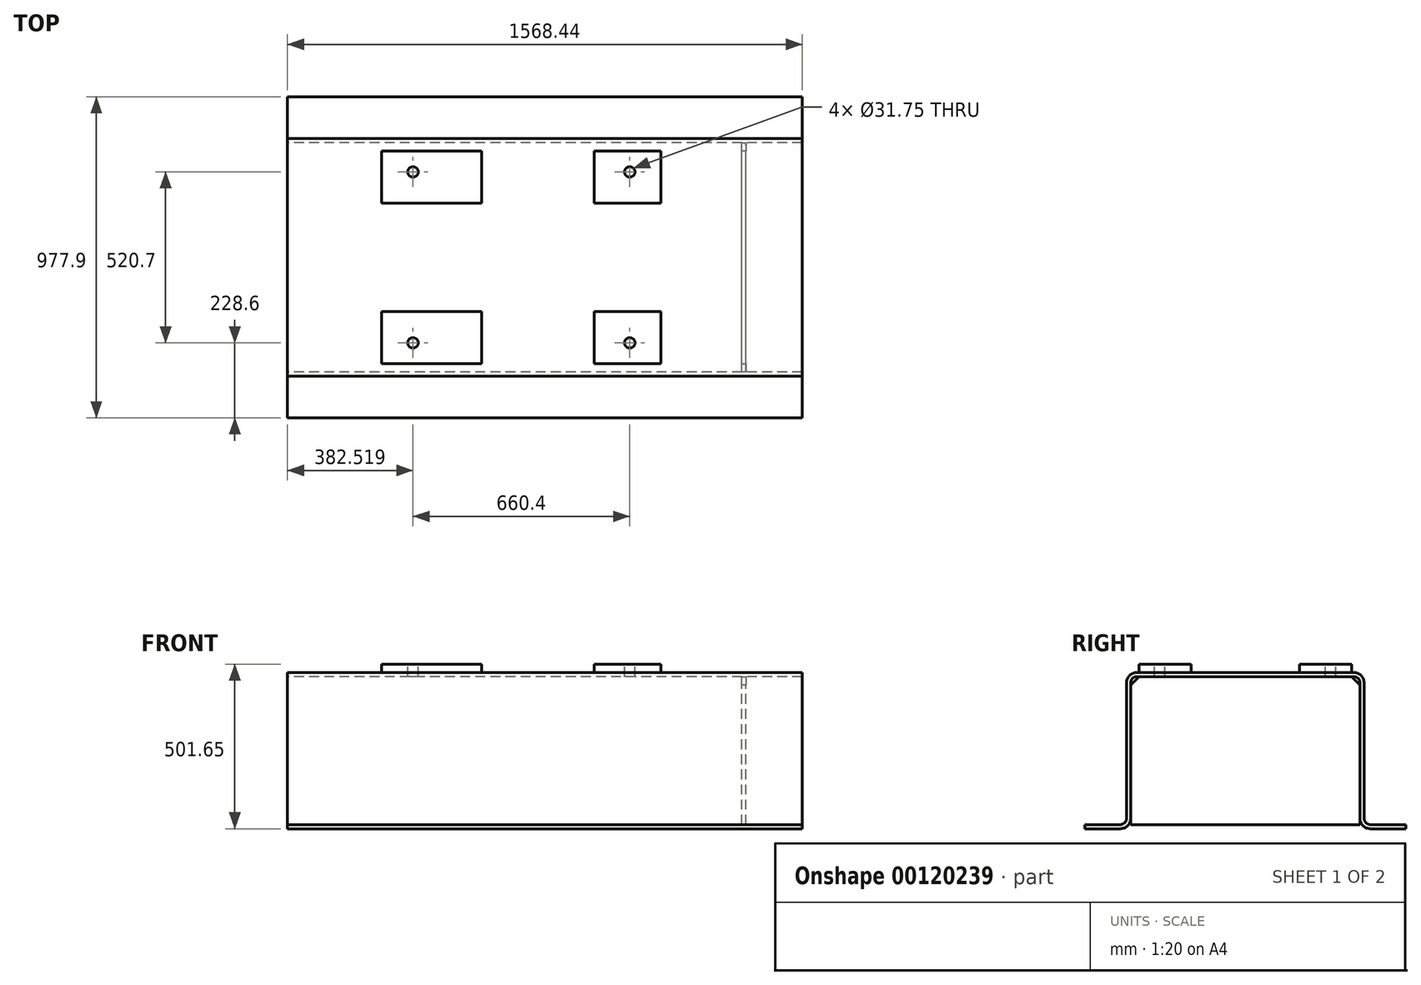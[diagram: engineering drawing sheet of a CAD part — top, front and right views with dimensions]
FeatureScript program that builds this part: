
annotation { "Feature Type Name" : "Feature", "Feature Type Description" : "" }
export const myFeature = defineFeature(function(context is Context, id is Id, definition is map)
    precondition{}
    {
        {
            var Q0;
            Q0=qCreatedBy(makeId("Right.planeOp"),FACE);
            var sketch = newSketch(context, id + "F0", { "sketchPlane" : qUnion([Q0])});
            skLineSegment(sketch, "E0", {"start": v(-488.95, 0) * mm, "end": v(-381, 0) * mm});
            skLineSegment(sketch, "E1", {"start": v(0, -90.03) * mm, "end": v(0, 519.57) * mm, "construction": true});
            skLineSegment(sketch, "E2.0", {"start": v(-361.95, 31.75) * mm, "end": v(-361.95, 444.5) * mm});
            skLineSegment(sketch, "E3.0", {"start": v(-349.25, 31.75) * mm, "end": v(-349.25, 444.5) * mm});
            skPoint(sketch, "E4.orphan", {"position": v(-143.9, 0) * mm});
            skLineSegment(sketch, "E5.0", {"start": v(-488.95, 0) * mm, "end": v(-488.95, 12.7) * mm});
            skLineSegment(sketch, "E6.0", {"start": v(-488.95, 12.7) * mm, "end": v(-381, 12.7) * mm});
            skLineSegment(sketch, "E7.0", {"start": v(-330.2, 476.25) * mm, "end": v(0, 476.25) * mm});
            skLineSegment(sketch, "E8.0", {"start": v(-330.2, 463.55) * mm, "end": v(0, 463.55) * mm});
            skArc(sketch, "E9.filletArc", {"start": v(-381, 12.7) * mm, "mid": v(-367.53, 18.28) * mm, "end": v(-361.95, 31.75) * mm});
            skArc(sketch, "E10.filletArc", {"start": v(-330.2, 463.55) * mm, "mid": v(-343.67, 457.97) * mm, "end": v(-349.25, 444.5) * mm});
            skArc(sketch, "E11.filletArc", {"start": v(-330.2, 476.25) * mm, "mid": v(-352.65, 466.95) * mm, "end": v(-361.95, 444.5) * mm});
            skArc(sketch, "E12.filletArc", {"start": v(-381, 0) * mm, "mid": v(-358.55, 9.3) * mm, "end": v(-349.25, 31.75) * mm});
            skArc(sketch, "E13.MirrorCS", {"start": v(330.2, 463.55) * mm, "mid": v(343.67, 457.97) * mm, "end": v(349.25, 444.5) * mm});
            skLineSegment(sketch, "E14.MirrorCS", {"start": v(361.95, 31.75) * mm, "end": v(361.95, 444.5) * mm});
            skLineSegment(sketch, "E15.MirrorCS", {"start": v(349.25, 31.75) * mm, "end": v(349.25, 444.5) * mm});
            skArc(sketch, "E16.MirrorCS", {"start": v(330.2, 476.25) * mm, "mid": v(352.65, 466.95) * mm, "end": v(361.95, 444.5) * mm});
            skLineSegment(sketch, "E17.MirrorCS", {"start": v(330.2, 463.55) * mm, "end": v(0, 463.55) * mm});
            skLineSegment(sketch, "E18.MirrorCS", {"start": v(330.2, 476.25) * mm, "end": v(0, 476.25) * mm});
            skArc(sketch, "E19.MirrorCS", {"start": v(381, 12.7) * mm, "mid": v(367.53, 18.28) * mm, "end": v(361.95, 31.75) * mm});
            skLineSegment(sketch, "E20.MirrorCS", {"start": v(488.95, 0) * mm, "end": v(488.95, 12.7) * mm});
            skLineSegment(sketch, "E21.MirrorCS", {"start": v(488.95, 0) * mm, "end": v(381, 0) * mm});
            skArc(sketch, "E22.MirrorCS", {"start": v(381, 0) * mm, "mid": v(358.55, 9.3) * mm, "end": v(349.25, 31.75) * mm});
            skLineSegment(sketch, "E23.MirrorCS", {"start": v(488.95, 12.7) * mm, "end": v(381, 12.7) * mm});
            skSolve(sketch);
        }
        {
            var Q0;
            Q0 = qSketchRegion(id + "F0", true);
            extrude(context, id + "F1", {"entities" : qUnion([Q0]), "endBound" : BoundingType.SYMMETRIC, "depth" : 1568.45 * mm});
        }
        {
            var Q0;
            Q0=makeQuery(id+"F1.opExtrude","SWEPT_FACE",FACE,{"disambiguationData":[OSD([sQuery(id+"F0.wireOp",EDGE,"E7.0"),sQuery(id+"F0.wireOp",EDGE,"E18.MirrorCS")])]});
            var sketch = newSketch(context, id + "F2", { "sketchPlane" : qUnion([Q0])});
            skLineSegment(sketch, "E24.0", {"start": v(784.23, 330.2) * mm, "end": v(784.23, -330.2) * mm, "construction": true});
            skLineSegment(sketch, "E25.0", {"start": v(582.55, 330.2) * mm, "end": v(582.55, -330.2) * mm, "construction": true});
            skLineSegment(sketch, "E26.0", {"start": v(-790.58, 336.55) * mm, "end": v(-790.58, -336.55) * mm, "construction": true});
            skLineSegment(sketch, "E26.1", {"start": v(790.58, 336.55) * mm, "end": v(-790.58, 336.55) * mm, "construction": true});
            skLineSegment(sketch, "E26.2", {"start": v(790.58, -336.55) * mm, "end": v(790.58, 336.55) * mm, "construction": true});
            skLineSegment(sketch, "E26.3", {"start": v(-790.58, -336.55) * mm, "end": v(790.58, -336.55) * mm, "construction": true});
            skLineSegment(sketch, "E27.0", {"start": v(-71.5, 330.2) * mm, "end": v(-71.5, -330.2) * mm, "construction": true});
            skLineSegment(sketch, "E28.0", {"start": v(150.75, 330.2) * mm, "end": v(150.75, -330.2) * mm, "construction": true});
            skLineSegment(sketch, "E29.0", {"start": v(-192.15, 330.2) * mm, "end": v(-192.15, -330.2) * mm, "construction": true});
            skLineSegment(sketch, "E30.0", {"start": v(-496.95, 330.2) * mm, "end": v(-496.95, -330.2) * mm, "construction": true});
            skLineSegment(sketch, "E31.0", {"start": v(353.95, 330.2) * mm, "end": v(353.95, -330.2) * mm, "construction": true});
            skLineSegment(sketch, "E32", {"start": v(-907.39, 0) * mm, "end": v(912.67, 0) * mm, "construction": true});
            skLineSegment(sketch, "E33.0", {"start": v(-907.39, 165.1) * mm, "end": v(912.67, 165.1) * mm, "construction": true});
            skLineSegment(sketch, "E34.bottom", {"start": v(-192.15, 165.1) * mm, "end": v(-496.95, 165.1) * mm});
            skLineSegment(sketch, "E34.top", {"start": v(-192.15, 323.85) * mm, "end": v(-496.95, 323.85) * mm});
            skLineSegment(sketch, "E34.left", {"start": v(-192.15, 165.1) * mm, "end": v(-192.15, 323.85) * mm});
            skLineSegment(sketch, "E34.right", {"start": v(-496.95, 165.1) * mm, "end": v(-496.95, 323.85) * mm});
            skLineSegment(sketch, "E35.bottom", {"start": v(150.75, 165.1) * mm, "end": v(353.95, 165.1) * mm});
            skLineSegment(sketch, "E35.top", {"start": v(150.75, 323.85) * mm, "end": v(353.95, 323.85) * mm});
            skLineSegment(sketch, "E35.left", {"start": v(150.75, 165.1) * mm, "end": v(150.75, 323.85) * mm});
            skLineSegment(sketch, "E35.right", {"start": v(353.95, 165.1) * mm, "end": v(353.95, 323.85) * mm});
            skLineSegment(sketch, "E36.MirrorCS", {"start": v(-192.15, -165.1) * mm, "end": v(-192.15, -323.85) * mm});
            skLineSegment(sketch, "E37.MirrorCS", {"start": v(353.95, -165.1) * mm, "end": v(353.95, -323.85) * mm});
            skLineSegment(sketch, "E38.MirrorCS", {"start": v(150.75, -323.85) * mm, "end": v(353.95, -323.85) * mm});
            skLineSegment(sketch, "E39.MirrorCS", {"start": v(-496.95, -165.1) * mm, "end": v(-496.95, -323.85) * mm});
            skLineSegment(sketch, "E40.MirrorCS", {"start": v(150.75, -165.1) * mm, "end": v(150.75, -323.85) * mm});
            skLineSegment(sketch, "E41.MirrorCS", {"start": v(150.75, -165.1) * mm, "end": v(353.95, -165.1) * mm});
            skLineSegment(sketch, "E42.MirrorCS", {"start": v(-192.15, -323.85) * mm, "end": v(-496.95, -323.85) * mm});
            skLineSegment(sketch, "E43.MirrorCS", {"start": v(-192.15, -165.1) * mm, "end": v(-496.95, -165.1) * mm});
            skSolve(sketch);
        }
        {
            var Q0;
            Q0 = qSketchRegion(id + "F2", true);
            extrude(context, id + "F3", {"entities" : qUnion([Q0]), "operationType" : NewBodyOperationType.ADD, "depth" : 25.4 * mm});
        }
        {
            var Q0;
            Q0=makeQuery(id+"F3.opExtrude","CAP_FACE",FACE,{"disambiguationData":[OSD([sQuery(id+"F2.wireOp",EDGE,"E34.bottom"),sQuery(id+"F2.wireOp",EDGE,"E34.top"),sQuery(id+"F2.wireOp",EDGE,"E34.left"),sQuery(id+"F2.wireOp",EDGE,"E34.right")])],"isStart":false});
            var sketch = newSketch(context, id + "F4", { "sketchPlane" : qUnion([Q0])});
            skLineSegment(sketch, "E44.0", {"start": v(-907.39, 0) * mm, "end": v(912.67, 0) * mm, "construction": true});
            skLineSegment(sketch, "E45.0", {"start": v(-71.5, 330.2) * mm, "end": v(-71.5, -330.2) * mm, "construction": true});
            skLineSegment(sketch, "E46.0", {"start": v(-907.39, 260.35) * mm, "end": v(912.67, 260.35) * mm, "construction": true});
            skLineSegment(sketch, "E47.0", {"start": v(-401.7, 330.2) * mm, "end": v(-401.7, -330.2) * mm, "construction": true});
            skPoint(sketch, "E48", {"position": v(-401.7, 260.35) * mm});
            skPoint(sketch, "E49.MirrorP", {"position": v(258.7, 260.35) * mm});
            skPoint(sketch, "E50.MirrorP", {"position": v(-401.7, -260.35) * mm});
            skPoint(sketch, "E51.MirrorP", {"position": v(258.7, -260.35) * mm});
            skSolve(sketch);
        }
        {
            var Q0;
            Q0=sQuery(id+"F4.wireOp",VERTEX,"E48");
            var Q1;
            Q1=sQuery(id+"F4.wireOp",VERTEX,"E49.MirrorP");
            var Q2;
            Q2=sQuery(id+"F4.wireOp",VERTEX,"E51.MirrorP");
            var Q3;
            Q3=sQuery(id+"F4.wireOp",VERTEX,"E50.MirrorP");
            var Q4;
            Q4=makeQuery(id+"F1.opExtrude","SWEPT_BODY",BODY,{"disambiguationData":[OSD([sQuery(id+"F0.wireOp",EDGE,"E0"),sQuery(id+"F0.wireOp",EDGE,"E2.0"),sQuery(id+"F0.wireOp",EDGE,"E3.0"),sQuery(id+"F0.wireOp",EDGE,"E5.0"),sQuery(id+"F0.wireOp",EDGE,"E6.0"),sQuery(id+"F0.wireOp",EDGE,"E7.0"),sQuery(id+"F0.wireOp",EDGE,"E8.0"),sQuery(id+"F0.wireOp",EDGE,"E9.filletArc"),sQuery(id+"F0.wireOp",EDGE,"E10.filletArc"),sQuery(id+"F0.wireOp",EDGE,"E11.filletArc"),sQuery(id+"F0.wireOp",EDGE,"E12.filletArc"),sQuery(id+"F0.wireOp",EDGE,"E13.MirrorCS"),sQuery(id+"F0.wireOp",EDGE,"E16.MirrorCS"),sQuery(id+"F0.wireOp",EDGE,"E17.MirrorCS"),sQuery(id+"F0.wireOp",EDGE,"E18.MirrorCS"),sQuery(id+"F0.wireOp",EDGE,"E19.MirrorCS"),sQuery(id+"F0.wireOp",EDGE,"E20.MirrorCS"),sQuery(id+"F0.wireOp",EDGE,"E21.MirrorCS"),sQuery(id+"F0.wireOp",EDGE,"E22.MirrorCS"),sQuery(id+"F0.wireOp",EDGE,"E23.MirrorCS"),sQuery(id+"F0.wireOp",EDGE,"E14.MirrorCS"),sQuery(id+"F0.wireOp",EDGE,"E15.MirrorCS")])]});
            hole(context, id + "F5", {"style" : HoleStyle.SIMPLE, "endStyle" : HoleEndStyle.THROUGH, "holeDiameter" : 31.75 * mm, "locations" : qUnion([Q0, Q1, Q2, Q3]), "scope" : qUnion([Q4]), "isTappedThrough" : true});
        }
        {
            var Q0;
            Q0=makeQuery(id+"F1.opExtrude","SWEPT_FACE",FACE,{"disambiguationData":[OSD([sQuery(id+"F0.wireOp",EDGE,"E8.0"),sQuery(id+"F0.wireOp",EDGE,"E17.MirrorCS")])]});
            var sketch = newSketch(context, id + "F6", { "sketchPlane" : qUnion([Q0])});
            skLineSegment(sketch, "E52.0", {"start": v(784.23, 349.25) * mm, "end": v(784.23, -349.25) * mm, "construction": true});
            skLineSegment(sketch, "E53.0.1", {"start": v(-784.23, 349.25) * mm, "end": v(784.23, 349.25) * mm, "construction": true});
            skLineSegment(sketch, "E53.0.3", {"start": v(784.23, 349.25) * mm, "end": v(-784.23, 349.25) * mm, "construction": true});
            skLineSegment(sketch, "E54.0.1", {"start": v(-784.23, -349.25) * mm, "end": v(784.23, -349.25) * mm, "construction": true});
            skLineSegment(sketch, "E54.0.3", {"start": v(784.23, -349.25) * mm, "end": v(-784.23, -349.25) * mm, "construction": true});
            skPoint(sketch, "E55.orphan", {"position": v(784.23, 330.2) * mm});
            skPoint(sketch, "E56.orphan", {"position": v(784.23, -330.2) * mm});
            skLineSegment(sketch, "E57.0", {"start": v(612.78, 349.25) * mm, "end": v(612.78, -349.25) * mm});
            skLineSegment(sketch, "E58.0", {"start": v(600.08, 349.25) * mm, "end": v(600.08, -349.25) * mm});
            skLineSegment(sketch, "E59", {"start": v(600.08, 349.25) * mm, "end": v(612.78, 349.25) * mm});
            skLineSegment(sketch, "E60", {"start": v(612.78, -349.25) * mm, "end": v(600.08, -349.25) * mm});
            skSolve(sketch);
        }
        {
            var Q0;
            Q0 = qSketchRegion(id + "F6", true);
            extrude(context, id + "F7", {"entities" : qUnion([Q0]), "depth" : 450.85 * mm});
        }
        {
            var Q0;
            Q0=makeQuery(id+"F7.opExtrude","CAP_EDGE",EDGE,{"disambiguationData":[OSD([sQuery(id+"F6.wireOp",EDGE,"E60")])],"isStart":true});
            var Q1;
            Q1=makeQuery(id+"F7.opExtrude","CAP_EDGE",EDGE,{"disambiguationData":[OSD([sQuery(id+"F6.wireOp",EDGE,"E59")])],"isStart":true});
            chamfer(context, id + "F8", {"entities" : qUnion([Q0, Q1]), "width" : 25.4 * mm, "tangentPropagation" : true});
        }
    });
